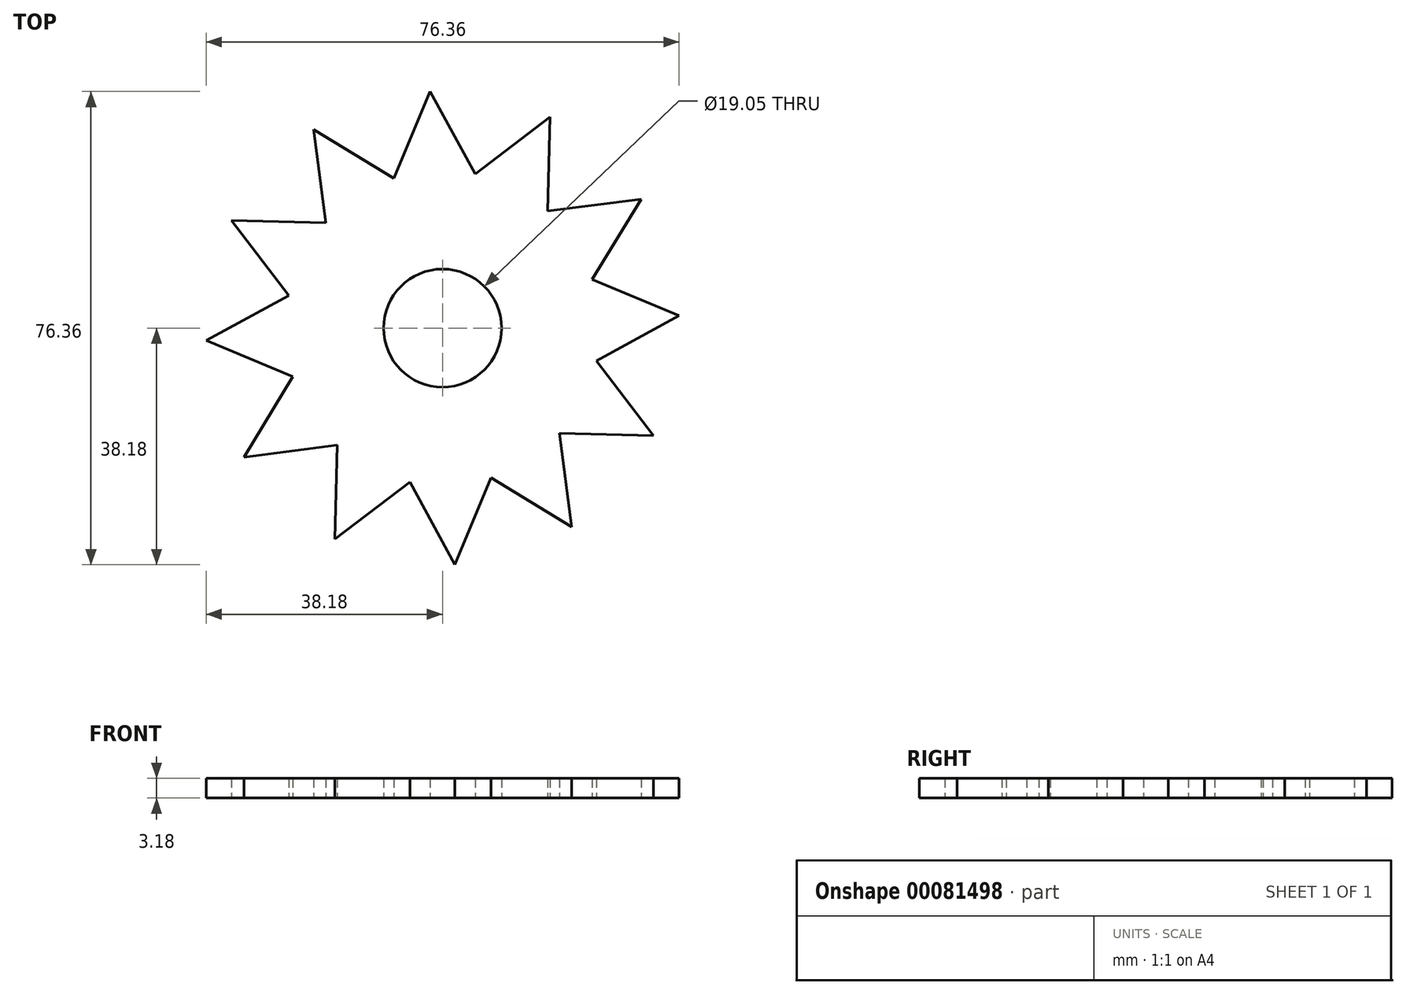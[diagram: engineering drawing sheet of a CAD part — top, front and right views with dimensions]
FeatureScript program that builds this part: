
annotation { "Feature Type Name" : "Feature", "Feature Type Description" : "" }
export const myFeature = defineFeature(function(context is Context, id is Id, definition is map)
    precondition{}
    {
        {
            var Q0;
            Q0=qCreatedBy(makeId("Top.planeOp"),FACE);
            var sketch = newSketch(context, id + "F0", { "sketchPlane" : qUnion([Q0])});
            skLineSegment(sketch, "E0", {"start": v(-7.85, 24.16) * mm, "end": v(-2, 38.18) * mm});
            skLineSegment(sketch, "E1", {"start": v(-2, 38.18) * mm, "end": v(5.28, 24.84) * mm});
            skLineSegment(sketch, "E2.1.0", {"start": v(-20.82, 32.06) * mm, "end": v(-7.85, 24.16) * mm});
            skLineSegment(sketch, "E2.1.1", {"start": v(-18.88, 17) * mm, "end": v(-20.82, 32.06) * mm});
            skLineSegment(sketch, "E2.2.0", {"start": v(-34.07, 17.36) * mm, "end": v(-18.88, 17) * mm});
            skLineSegment(sketch, "E2.2.1", {"start": v(-24.84, 5.28) * mm, "end": v(-34.07, 17.36) * mm});
            skLineSegment(sketch, "E2.3.0", {"start": v(-38.18, -2) * mm, "end": v(-24.84, 5.28) * mm});
            skLineSegment(sketch, "E2.3.1", {"start": v(-24.16, -7.85) * mm, "end": v(-38.18, -2) * mm});
            skLineSegment(sketch, "E2.4.0", {"start": v(-32.06, -20.82) * mm, "end": v(-24.16, -7.85) * mm});
            skLineSegment(sketch, "E2.4.1", {"start": v(-17, -18.88) * mm, "end": v(-32.06, -20.82) * mm});
            skLineSegment(sketch, "E2.5.0", {"start": v(-17.36, -34.07) * mm, "end": v(-17, -18.88) * mm});
            skLineSegment(sketch, "E2.5.1", {"start": v(-5.28, -24.84) * mm, "end": v(-17.36, -34.07) * mm});
            skLineSegment(sketch, "E2.6.0", {"start": v(2, -38.18) * mm, "end": v(-5.28, -24.84) * mm});
            skLineSegment(sketch, "E2.6.1", {"start": v(7.85, -24.16) * mm, "end": v(2, -38.18) * mm});
            skLineSegment(sketch, "E2.7.0", {"start": v(20.82, -32.06) * mm, "end": v(7.85, -24.16) * mm});
            skLineSegment(sketch, "E2.7.1", {"start": v(18.88, -17) * mm, "end": v(20.82, -32.06) * mm});
            skLineSegment(sketch, "E2.8.0", {"start": v(34.07, -17.36) * mm, "end": v(18.88, -17) * mm});
            skLineSegment(sketch, "E2.8.1", {"start": v(24.84, -5.28) * mm, "end": v(34.07, -17.36) * mm});
            skLineSegment(sketch, "E2.9.0", {"start": v(38.18, 2) * mm, "end": v(24.84, -5.28) * mm});
            skLineSegment(sketch, "E2.9.1", {"start": v(24.16, 7.85) * mm, "end": v(38.18, 2) * mm});
            skPoint(sketch, "E2.center", {"position": v(0, 0) * mm});
            skCircle(sketch, "E3", {"center": v(0, 0) * mm, "radius": 9.53 * mm});
            skLineSegment(sketch, "E4.2.10.0", {"start": v(32.06, 20.82) * mm, "end": v(24.16, 7.85) * mm});
            skLineSegment(sketch, "E4.3.10.0", {"start": v(17, 18.88) * mm, "end": v(32.06, 20.82) * mm});
            skLineSegment(sketch, "E4.2.11.0", {"start": v(17.36, 34.07) * mm, "end": v(17, 18.88) * mm});
            skLineSegment(sketch, "E4.3.11.0", {"start": v(5.28, 24.84) * mm, "end": v(17.36, 34.07) * mm});
            skSolve(sketch);
        }
        {
            var Q0;
            Q0=makeQuery(id+"F0.imprint","IMPRINT",FACE,{"disambiguationData":[TD([[makeQuery(id+"F0.imprint","IMPRINT",EDGE,{"derivedFrom":sQuery(id+"F0.wireOp",EDGE,"E0")}),-1.0]])]});
            extrude(context, id + "F1", {"entities" : qUnion([Q0]), "depth" : 3.17 * mm});
        }
    });
